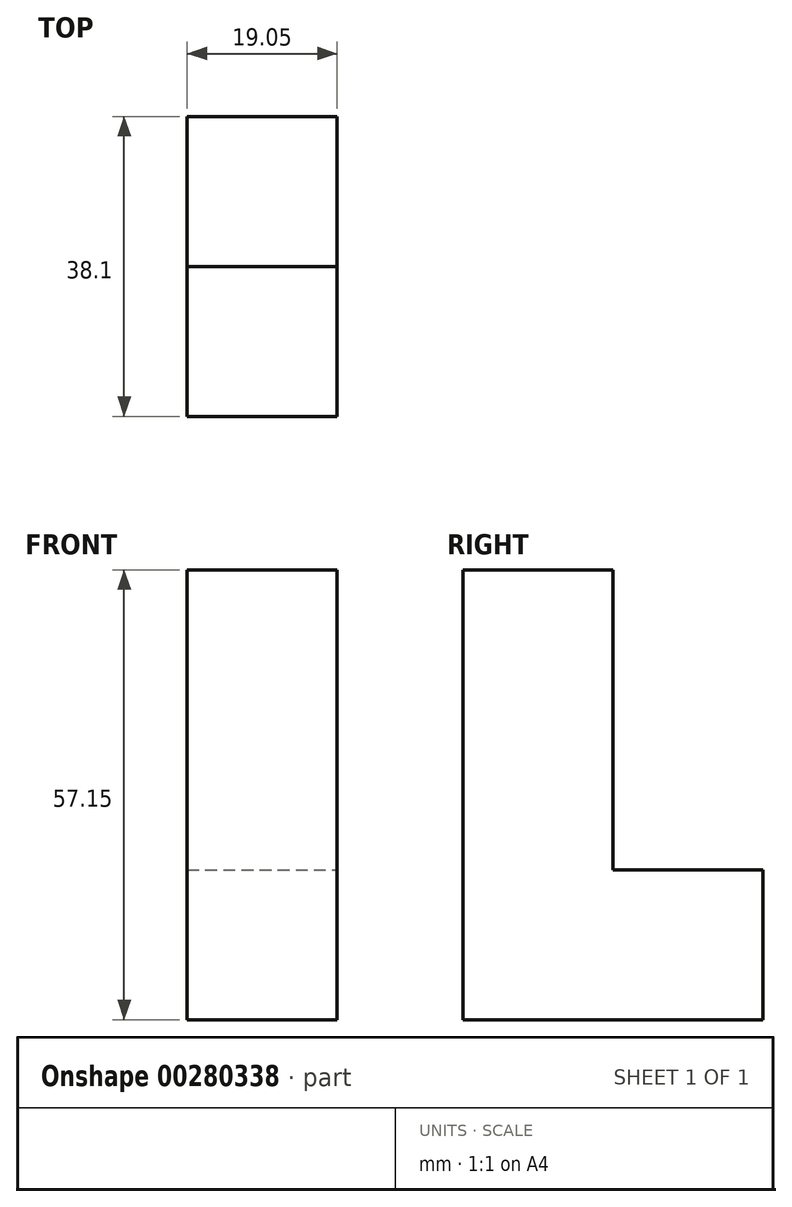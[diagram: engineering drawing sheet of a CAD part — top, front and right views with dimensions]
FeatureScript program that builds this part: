
annotation { "Feature Type Name" : "Feature", "Feature Type Description" : "" }
export const myFeature = defineFeature(function(context is Context, id is Id, definition is map)
    precondition{}
    {
        {
            var Q0;
            Q0=qCreatedBy(makeId("Top.planeOp"),FACE);
            var sketch = newSketch(context, id + "F0", { "sketchPlane" : qUnion([Q0])});
            skLineSegment(sketch, "E0.bottom", {"start": v(0, 0) * mm, "end": v(19.05, 0) * mm});
            skLineSegment(sketch, "E0.top", {"start": v(0, 38.1) * mm, "end": v(19.05, 38.1) * mm});
            skLineSegment(sketch, "E0.left", {"start": v(0, 0) * mm, "end": v(0, 38.1) * mm});
            skLineSegment(sketch, "E0.right", {"start": v(19.05, 0) * mm, "end": v(19.05, 38.1) * mm});
            skSolve(sketch);
        }
        {
            var Q0;
            Q0 = qSketchRegion(id + "F0", true);
            extrude(context, id + "F1", {"entities" : qUnion([Q0]), "depth" : 57.15 * mm});
        }
        {
            var Q0;
            Q0=makeQuery(id+"F1.opExtrude","CAP_FACE",FACE,{"disambiguationData":[OSD([sQuery(id+"F0.wireOp",EDGE,"E0.bottom"),sQuery(id+"F0.wireOp",EDGE,"E0.top"),sQuery(id+"F0.wireOp",EDGE,"E0.left"),sQuery(id+"F0.wireOp",EDGE,"E0.right")])],"isStart":false});
            var sketch = newSketch(context, id + "F2", { "sketchPlane" : qUnion([Q0])});
            skLineSegment(sketch, "E1.bottom", {"start": v(0, 38.1) * mm, "end": v(19.05, 38.1) * mm});
            skLineSegment(sketch, "E1.top", {"start": v(0, 19.05) * mm, "end": v(19.05, 19.05) * mm});
            skLineSegment(sketch, "E1.left", {"start": v(0, 38.1) * mm, "end": v(0, 19.05) * mm});
            skLineSegment(sketch, "E1.right", {"start": v(19.05, 38.1) * mm, "end": v(19.05, 19.05) * mm});
            skSolve(sketch);
        }
        {
            var Q0;
            {var subQ0=sQuery(id+"F2.wireOp",EDGE,"E1.top");Q0=makeQuery(id+"F2.imprint","IMPRINT",FACE,{"disambiguationData":[TD([[makeQuery(id+"F2.imprint","IMPRINT",EDGE,{"derivedFrom":subQ0}),-1.0]])]});}
            var sketch = newSketch(context, id + "F3", { "sketchPlane" : qUnion([Q0])});
            skSolve(sketch);
        }
        {
            var Q0;
            Q0 = qSketchRegion(id + "F3", true);
            var Q1;
            Q1=makeQuery(id+"F2.imprint","IMPRINT",FACE,{"disambiguationData":[TD([[makeQuery(id+"F2.imprint","IMPRINT",EDGE,{"derivedFrom":sQuery(id+"F2.wireOp",EDGE,"E1.bottom")}),-1.0]])]});
            extrude(context, id + "F4", {"entities" : qUnion([Q0, Q1]), "operationType" : NewBodyOperationType.REMOVE, "oppositeDirection" : true, "depth" : 38.1 * mm});
        }
    });
